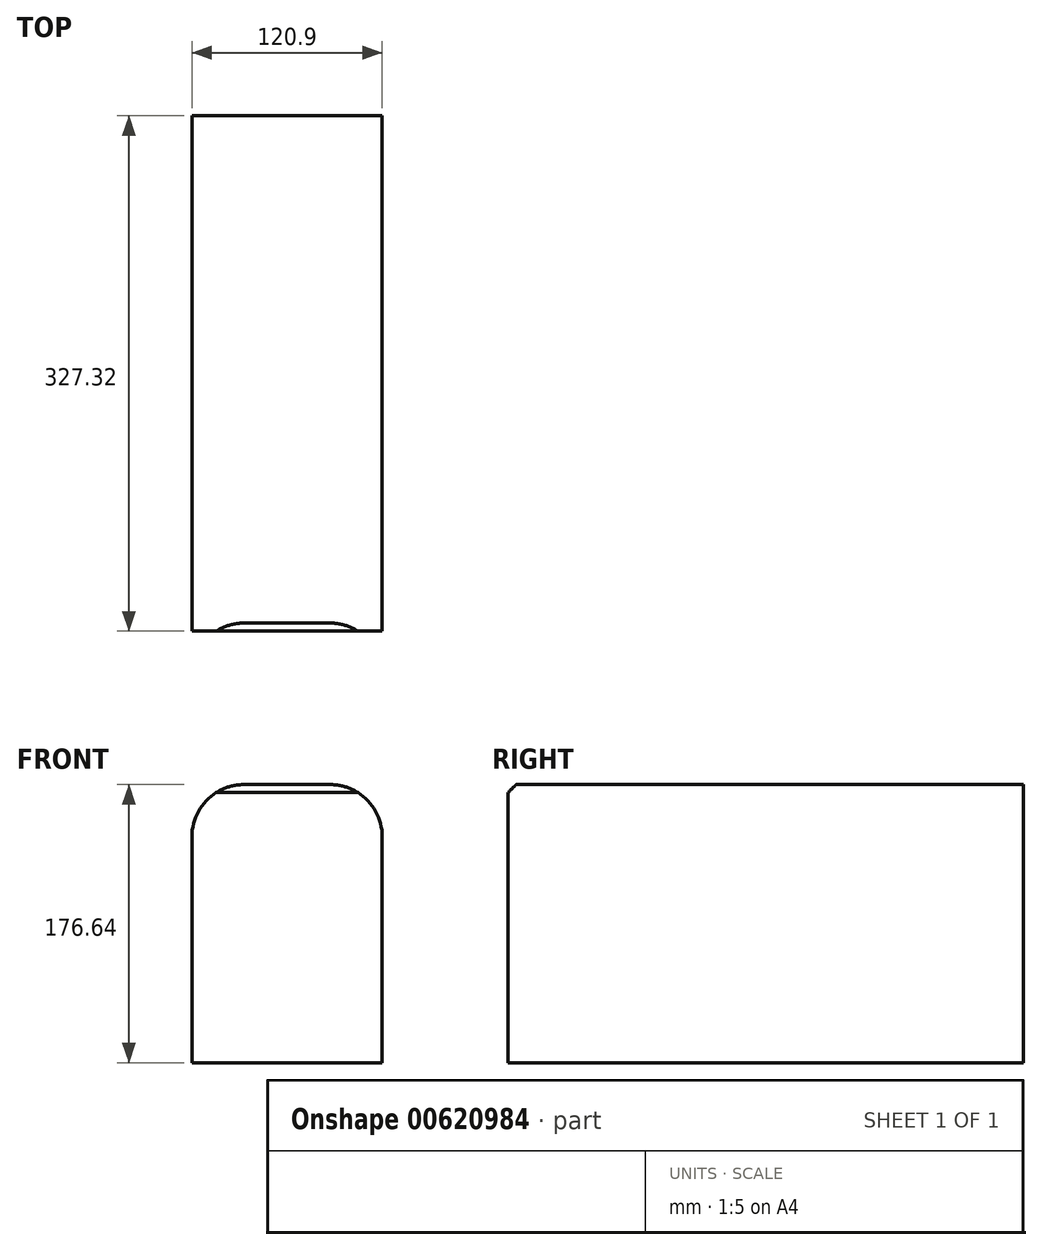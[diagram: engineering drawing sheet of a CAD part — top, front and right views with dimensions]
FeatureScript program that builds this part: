
annotation { "Feature Type Name" : "Feature", "Feature Type Description" : "" }
export const myFeature = defineFeature(function(context is Context, id is Id, definition is map)
    precondition{}
    {
        {
            var Q0;
            Q0=qCreatedBy(makeId("Right.planeOp"),FACE);
            var sketch = newSketch(context, id + "F0", { "sketchPlane" : qUnion([Q0])});
            skLineSegment(sketch, "E0.bottom", {"start": v(-51.35, 22.42) * mm, "end": v(275.97, 22.42) * mm});
            skLineSegment(sketch, "E0.top", {"start": v(-51.35, -154.22) * mm, "end": v(275.97, -154.22) * mm});
            skLineSegment(sketch, "E0.left", {"start": v(-51.35, 22.42) * mm, "end": v(-51.35, -154.22) * mm});
            skLineSegment(sketch, "E0.right", {"start": v(275.97, 22.42) * mm, "end": v(275.97, -154.22) * mm});
            skSolve(sketch);
        }
        {
            var Q0;
            Q0 = qSketchRegion(id + "F0", true);
            extrude(context, id + "F1", {"entities" : qUnion([Q0]), "depth" : 120.9 * mm, "offsetDistance" : 25.4 * mm});
        }
        {
            var Q0;
            Q0=makeQuery(id+"F1.opExtrude","SWEPT_EDGE",EDGE,{"disambiguationData":[OSD([sQuery(id+"F0.wireOp",EDGE,"E0.bottom"),sQuery(id+"F0.wireOp",EDGE,"E0.left")])]});
            chamfer(context, id + "F2", {"entities" : qUnion([Q0]), "width" : 5.08 * mm, "tangentPropagation" : true});
        }
        {
            var Q0;
            Q0=makeQuery(id+"F1.opExtrude","CAP_EDGE",EDGE,{"disambiguationData":[OSD([sQuery(id+"F0.wireOp",EDGE,"E0.bottom")])],"isStart":false});
            var Q1;
            Q1=makeQuery(id+"F1.opExtrude","CAP_EDGE",EDGE,{"disambiguationData":[OSD([sQuery(id+"F0.wireOp",EDGE,"E0.bottom")])],"isStart":true});
            fillet(context, id + "F3", {"entities" : qUnion([Q0, Q1]), "radius" : 33.1 * mm, "tangentPropagation" : true, "allowEdgeOverflow" : false});
        }
    });
